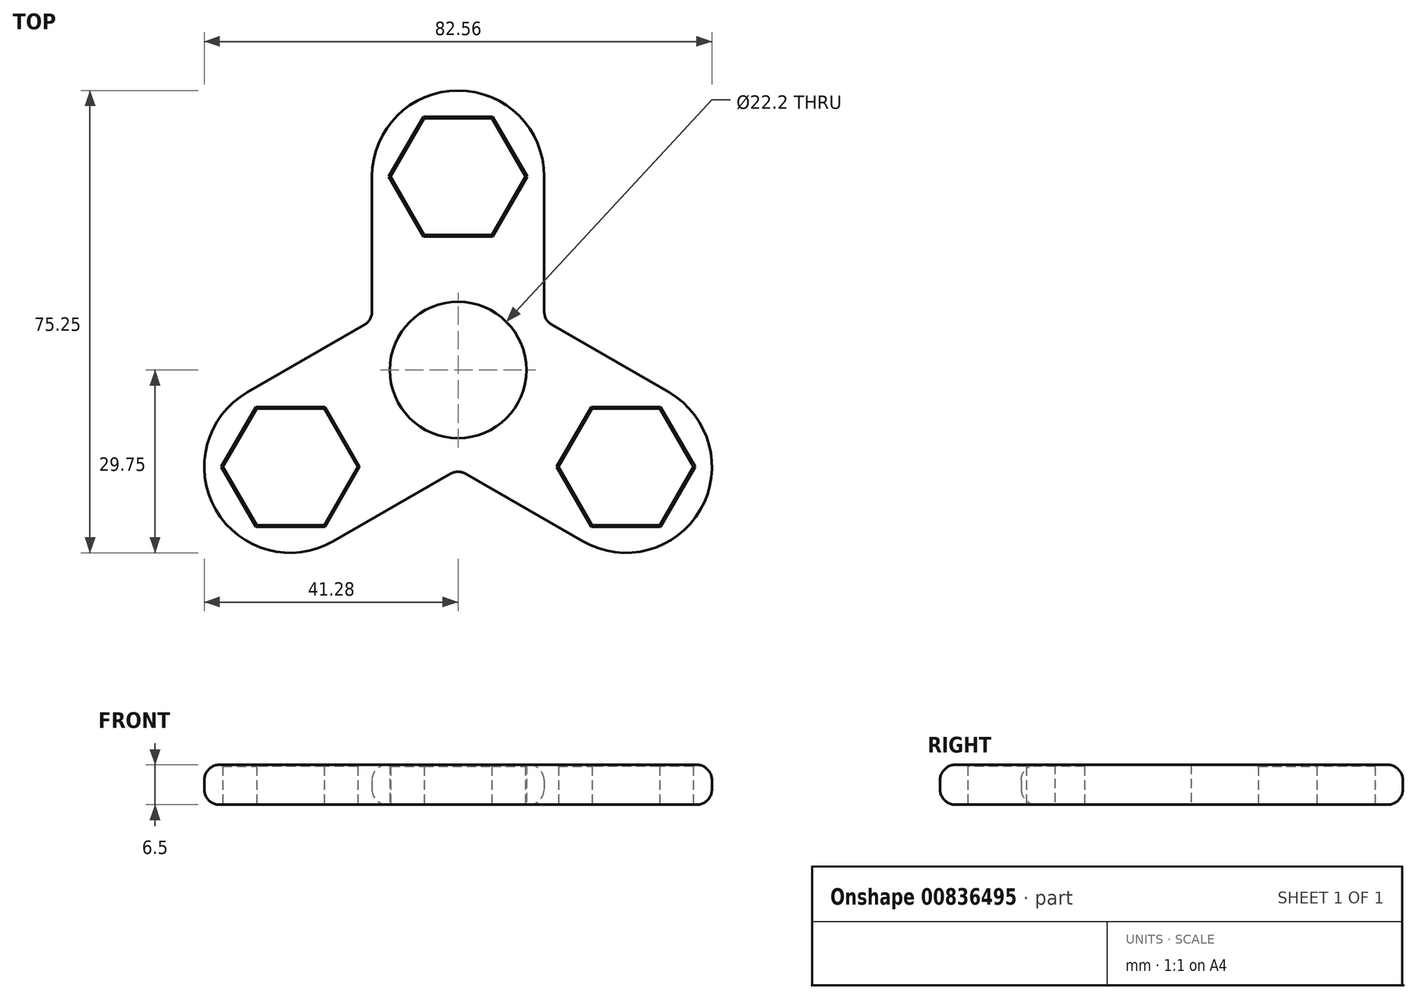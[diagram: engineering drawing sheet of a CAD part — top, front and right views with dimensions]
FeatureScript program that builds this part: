
annotation { "Feature Type Name" : "Feature", "Feature Type Description" : "" }
export const myFeature = defineFeature(function(context is Context, id is Id, definition is map)
    precondition{}
    {
        {
            var Q0;
            Q0=qCreatedBy(makeId("Top.planeOp"),FACE);
            var sketch = newSketch(context, id + "F0", { "sketchPlane" : qUnion([Q0])});
            skCircle(sketch, "E0", {"center": v(0, 0) * mm, "radius": 11.1 * mm});
            skCircle(sketch, "E1", {"center": v(0, 0) * mm, "radius": 14 * mm});
            skCircle(sketch, "E2.cCircle", {"center": v(0, 31.5) * mm, "radius": 9.5 * mm, "construction": true});
            skLineSegment(sketch, "E2.0", {"start": v(5.48, 22) * mm, "end": v(-5.48, 22) * mm});
            skLineSegment(sketch, "E2.1", {"start": v(-5.48, 22) * mm, "end": v(-10.97, 31.5) * mm});
            skLineSegment(sketch, "E2.2", {"start": v(-10.97, 31.5) * mm, "end": v(-5.48, 41) * mm});
            skLineSegment(sketch, "E2.3", {"start": v(-5.48, 41) * mm, "end": v(5.48, 41) * mm});
            skLineSegment(sketch, "E2.4", {"start": v(5.48, 41) * mm, "end": v(10.97, 31.5) * mm});
            skLineSegment(sketch, "E2.5", {"start": v(10.97, 31.5) * mm, "end": v(5.48, 22) * mm});
            skPoint(sketch, "E2.0.midPoint", {"position": v(0, 22) * mm});
            skCircle(sketch, "E3", {"center": v(0, 31.5) * mm, "radius": 14 * mm});
            skLineSegment(sketch, "E4", {"start": v(-14, 31.5) * mm, "end": v(-14, 0) * mm});
            skLineSegment(sketch, "E5.MirrorCS", {"start": v(14, 31.5) * mm, "end": v(14, 0) * mm});
            skLineSegment(sketch, "E6.1.0", {"start": v(-16.31, -15.75) * mm, "end": v(-21.8, -25.25) * mm});
            skCircle(sketch, "E6.1.1", {"center": v(-27.28, -15.75) * mm, "radius": 14 * mm});
            skLineSegment(sketch, "E6.1.2", {"start": v(-20.28, -27.87) * mm, "end": v(7, -12.12) * mm});
            skLineSegment(sketch, "E6.1.3", {"start": v(-34.28, -3.63) * mm, "end": v(-7, 12.12) * mm});
            skLineSegment(sketch, "E6.1.4", {"start": v(-32.76, -6.25) * mm, "end": v(-21.8, -6.25) * mm});
            skLineSegment(sketch, "E6.1.5", {"start": v(-21.8, -6.25) * mm, "end": v(-16.31, -15.75) * mm});
            skLineSegment(sketch, "E6.1.6", {"start": v(-38.25, -15.75) * mm, "end": v(-32.76, -6.25) * mm});
            skLineSegment(sketch, "E6.1.7", {"start": v(-32.76, -25.25) * mm, "end": v(-38.25, -15.75) * mm});
            skLineSegment(sketch, "E6.1.8", {"start": v(-21.8, -25.25) * mm, "end": v(-32.76, -25.25) * mm});
            skLineSegment(sketch, "E6.2.0", {"start": v(21.8, -6.25) * mm, "end": v(32.76, -6.25) * mm});
            skCircle(sketch, "E6.2.1", {"center": v(27.28, -15.75) * mm, "radius": 14 * mm});
            skLineSegment(sketch, "E6.2.2", {"start": v(34.28, -3.63) * mm, "end": v(7, 12.12) * mm});
            skLineSegment(sketch, "E6.2.3", {"start": v(20.28, -27.87) * mm, "end": v(-7, -12.12) * mm});
            skLineSegment(sketch, "E6.2.4", {"start": v(21.8, -25.25) * mm, "end": v(16.31, -15.75) * mm});
            skLineSegment(sketch, "E6.2.5", {"start": v(16.31, -15.75) * mm, "end": v(21.8, -6.25) * mm});
            skLineSegment(sketch, "E6.2.6", {"start": v(32.76, -25.25) * mm, "end": v(21.8, -25.25) * mm});
            skLineSegment(sketch, "E6.2.7", {"start": v(38.25, -15.75) * mm, "end": v(32.76, -25.25) * mm});
            skLineSegment(sketch, "E6.2.8", {"start": v(32.76, -6.25) * mm, "end": v(38.25, -15.75) * mm});
            skSolve(sketch);
        }
        {
            var Q0;
            Q0=qSketchRegion(id+"F0",true);
            var Q1;
            Q1=makeQuery(id+"F0.imprint","IMPRINT",FACE,{"disambiguationData":[TD([[makeQuery(id+"F0.imprint","IMPRINT",EDGE,{"derivedFrom":sQuery(id+"F0.wireOp",EDGE,"E0")}),-1.0]])]});
            extrude(context, id + "F1", {"entities" : qUnion([Q0, Q1]), "depth" : 6.5 * mm, "offsetDistance" : 25 * mm});
        }
        {
            var Q0;
            Q0=makeQuery(id+"F1.opExtrude","SWEPT_FACE",FACE,{"disambiguationData":[OSD([sQuery(id+"F0.wireOp",EDGE,"E6.1.2")])]});
            var Q1;
            Q1=makeQuery(id+"F1.opExtrude","SWEPT_FACE",FACE,{"disambiguationData":[OSD([sQuery(id+"F0.wireOp",EDGE,"E6.1.1")])]});
            var Q2;
            Q2=makeQuery(id+"F1.opExtrude","SWEPT_FACE",FACE,{"disambiguationData":[OSD([sQuery(id+"F0.wireOp",EDGE,"E6.2.3")])]});
            var Q3;
            Q3=makeQuery(id+"F1.opExtrude","SWEPT_FACE",FACE,{"disambiguationData":[OSD([sQuery(id+"F0.wireOp",EDGE,"E6.2.1")])]});
            var Q4;
            Q4=makeQuery(id+"F1.opExtrude","SWEPT_FACE",FACE,{"disambiguationData":[OSD([sQuery(id+"F0.wireOp",EDGE,"E6.2.2")])]});
            var Q5;
            Q5=makeQuery(id+"F1.opExtrude","SWEPT_FACE",FACE,{"disambiguationData":[OSD([sQuery(id+"F0.wireOp",EDGE,"E5.MirrorCS")])]});
            var Q6;
            Q6=makeQuery(id+"F1.opExtrude","SWEPT_FACE",FACE,{"disambiguationData":[OSD([sQuery(id+"F0.wireOp",EDGE,"E3")])]});
            var Q7;
            Q7=makeQuery(id+"F1.opExtrude","SWEPT_FACE",FACE,{"disambiguationData":[OSD([sQuery(id+"F0.wireOp",EDGE,"E4")])]});
            var Q8;
            Q8=makeQuery(id+"F1.opExtrude","SWEPT_FACE",FACE,{"disambiguationData":[OSD([sQuery(id+"F0.wireOp",EDGE,"E6.1.3")])]});
            fillet(context, id + "F2", {"entities" : qUnion([Q0, Q1, Q2, Q3, Q4, Q5, Q6, Q7, Q8]), "radius" : 2.5 * mm, "tangentPropagation" : true, "allowEdgeOverflow" : false});
        }
        {
            var Q0;
            Q0=makeQuery(id+"F1.opExtrude","CAP_EDGE",EDGE,{"disambiguationData":[OSD([sQuery(id+"F0.wireOp",EDGE,"E6.2.4")])],"isStart":false});
            var Q1;
            Q1=makeQuery(id+"F1.opExtrude","CAP_EDGE",EDGE,{"disambiguationData":[OSD([sQuery(id+"F0.wireOp",EDGE,"E6.2.5")])],"isStart":false});
            var Q2;
            Q2=makeQuery(id+"F1.opExtrude","CAP_EDGE",EDGE,{"disambiguationData":[OSD([sQuery(id+"F0.wireOp",EDGE,"E6.2.0")])],"isStart":false});
            var Q3;
            Q3=makeQuery(id+"F1.opExtrude","CAP_EDGE",EDGE,{"disambiguationData":[OSD([sQuery(id+"F0.wireOp",EDGE,"E6.2.8")])],"isStart":false});
            var Q4;
            Q4=makeQuery(id+"F1.opExtrude","CAP_EDGE",EDGE,{"disambiguationData":[OSD([sQuery(id+"F0.wireOp",EDGE,"E6.2.7")])],"isStart":false});
            var Q5;
            Q5=makeQuery(id+"F1.opExtrude","CAP_EDGE",EDGE,{"disambiguationData":[OSD([sQuery(id+"F0.wireOp",EDGE,"E6.2.6")])],"isStart":false});
            var Q6;
            Q6=makeQuery(id+"F1.opExtrude","CAP_EDGE",EDGE,{"disambiguationData":[OSD([sQuery(id+"F0.wireOp",EDGE,"E6.1.7")])],"isStart":false});
            var Q7;
            Q7=makeQuery(id+"F1.opExtrude","CAP_EDGE",EDGE,{"disambiguationData":[OSD([sQuery(id+"F0.wireOp",EDGE,"E6.1.6")])],"isStart":false});
            var Q8;
            Q8=makeQuery(id+"F1.opExtrude","CAP_EDGE",EDGE,{"disambiguationData":[OSD([sQuery(id+"F0.wireOp",EDGE,"E6.1.4")])],"isStart":false});
            var Q9;
            Q9=makeQuery(id+"F1.opExtrude","CAP_EDGE",EDGE,{"disambiguationData":[OSD([sQuery(id+"F0.wireOp",EDGE,"E6.1.5")])],"isStart":false});
            var Q10;
            Q10=makeQuery(id+"F1.opExtrude","CAP_EDGE",EDGE,{"disambiguationData":[OSD([sQuery(id+"F0.wireOp",EDGE,"E6.1.0")])],"isStart":false});
            var Q11;
            Q11=makeQuery(id+"F1.opExtrude","CAP_EDGE",EDGE,{"disambiguationData":[OSD([sQuery(id+"F0.wireOp",EDGE,"E6.1.8")])],"isStart":false});
            var Q12;
            Q12=makeQuery(id+"F1.opExtrude","CAP_EDGE",EDGE,{"disambiguationData":[OSD([sQuery(id+"F0.wireOp",EDGE,"E2.0")])],"isStart":false});
            var Q13;
            Q13=makeQuery(id+"F1.opExtrude","CAP_EDGE",EDGE,{"disambiguationData":[OSD([sQuery(id+"F0.wireOp",EDGE,"E2.5")])],"isStart":false});
            var Q14;
            Q14=makeQuery(id+"F1.opExtrude","CAP_EDGE",EDGE,{"disambiguationData":[OSD([sQuery(id+"F0.wireOp",EDGE,"E2.4")])],"isStart":false});
            var Q15;
            Q15=makeQuery(id+"F1.opExtrude","CAP_EDGE",EDGE,{"disambiguationData":[OSD([sQuery(id+"F0.wireOp",EDGE,"E2.3")])],"isStart":false});
            var Q16;
            Q16=makeQuery(id+"F1.opExtrude","CAP_EDGE",EDGE,{"disambiguationData":[OSD([sQuery(id+"F0.wireOp",EDGE,"E2.2")])],"isStart":false});
            var Q17;
            Q17=makeQuery(id+"F1.opExtrude","CAP_EDGE",EDGE,{"disambiguationData":[OSD([sQuery(id+"F0.wireOp",EDGE,"E2.1")])],"isStart":false});
            chamfer(context, id + "F3", {"entities" : qUnion([Q0, Q1, Q2, Q3, Q4, Q5, Q6, Q7, Q8, Q9, Q10, Q11, Q12, Q13, Q14, Q15, Q16, Q17]), "width" : 0.25 * mm, "tangentPropagation" : true});
        }
    });
